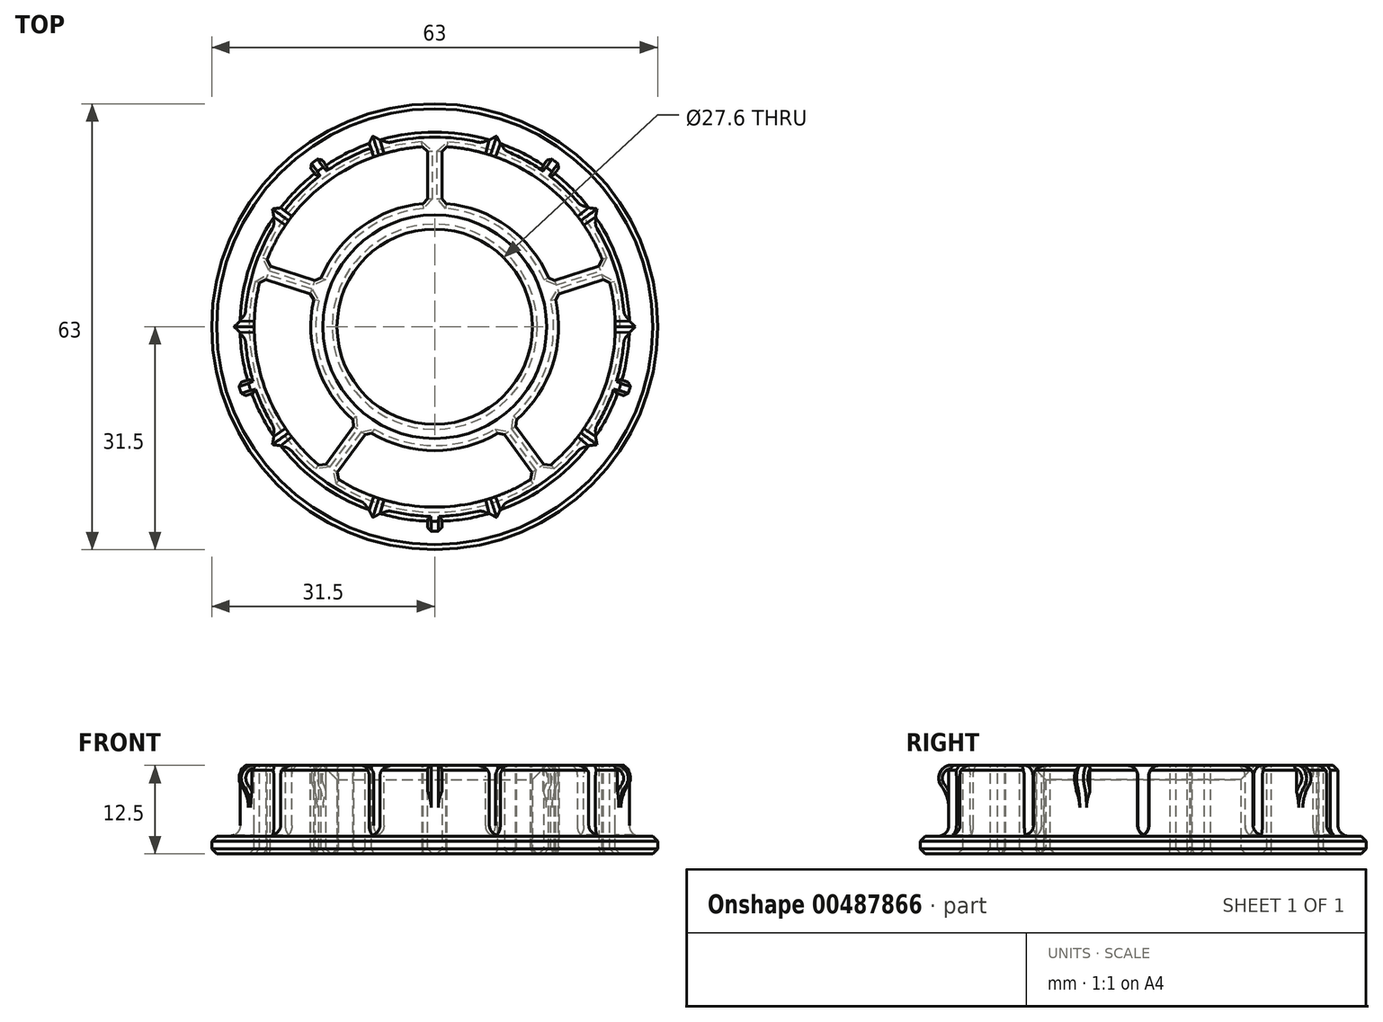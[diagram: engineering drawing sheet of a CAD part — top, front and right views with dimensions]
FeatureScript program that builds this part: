
annotation { "Feature Type Name" : "Feature", "Feature Type Description" : "" }
export const myFeature = defineFeature(function(context is Context, id is Id, definition is map)
    precondition{}
    {
        {
            var Q0;
            Q0=qCreatedBy(makeId("Front.planeOp"),FACE);
            var sketch = newSketch(context, id + "F0", { "sketchPlane" : qUnion([Q0])});
            skLineSegment(sketch, "E0", {"start": v(0, 0) * mm, "end": v(-63, 0) * mm, "construction": true});
            skLineSegment(sketch, "E1", {"start": v(-31.5, 0) * mm, "end": v(-31.5, 2.5) * mm});
            skLineSegment(sketch, "E2", {"start": v(-31.5, 2.5) * mm, "end": v(-27.5, 2.5) * mm});
            skLineSegment(sketch, "E3", {"start": v(-27.5, 2.5) * mm, "end": v(-27.5, 8.9) * mm});
            skLineSegment(sketch, "E4", {"start": v(-31.5, 0) * mm, "end": v(-13.8, 0) * mm});
            skLineSegment(sketch, "E5", {"start": v(-13.8, 0) * mm, "end": v(-13.8, 12.5) * mm});
            skLineSegment(sketch, "E6", {"start": v(-13.8, 12.5) * mm, "end": v(-27.5, 12.5) * mm});
            skLineSegment(sketch, "E7", {"start": v(0, 0) * mm, "end": v(0, 12.5) * mm, "construction": true});
            skLineSegment(sketch, "E8.0.MirrorCS", {"start": v(13.8, 0) * mm, "end": v(13.8, 12.5) * mm});
            skLineSegment(sketch, "E9.0.MirrorCS", {"start": v(13.8, 12.5) * mm, "end": v(27.5, 12.5) * mm});
            skLineSegment(sketch, "E10.0.MirrorCS", {"start": v(27.5, 2.5) * mm, "end": v(27.5, 12.5) * mm});
            skLineSegment(sketch, "E11.0.MirrorCS", {"start": v(31.5, 0) * mm, "end": v(31.5, 2.5) * mm});
            skLineSegment(sketch, "E12.0.MirrorCS", {"start": v(31.5, 0) * mm, "end": v(13.8, 0) * mm});
            skLineSegment(sketch, "E13.0.MirrorCS", {"start": v(31.5, 2.5) * mm, "end": v(27.5, 2.5) * mm});
            skArc(sketch, "E14", {"start": v(-27.5, 12.5) * mm, "mid": v(-28.9, 10.7) * mm, "end": v(-27.5, 8.9) * mm});
            skSolve(sketch);
        }
        {
            var Q0;
            Q0=makeQuery(id+"F0.imprint","IMPRINT",FACE,{"disambiguationData":[TD([[makeQuery(id+"F0.imprint","IMPRINT",EDGE,{"derivedFrom":sQuery(id+"F0.wireOp",EDGE,"E1")}),-1.0]])]});
            var Q1;
            Q1 = qSketchRegion(id + "F2", true);
            var Q2;
            Q2=sQuery(id+"F0.wireOp",EDGE,"E7");
            revolve(context, id + "F1", {"entities" : qUnion([Q0, Q1]), "axis" : qUnion([Q2]), "revolveType" : RevolveType.FULL});
        }
        {
            var Q0;
            Q0=makeQuery(id+"F1.opRevolve","SWEPT_FACE",FACE,{"disambiguationData":[OSD([sQuery(id+"F0.wireOp",EDGE,"E6")])]});
            var sketch = newSketch(context, id + "F2", { "sketchPlane" : qUnion([Q0])});
            skCircle(sketch, "E15.0", {"center": v(0, 0) * mm, "radius": 31.5 * mm});
            skCircle(sketch, "E15.1", {"center": v(0, 0) * mm, "radius": 13.8 * mm});
            skCircle(sketch, "E16.0", {"center": v(0, 0) * mm, "radius": 27.5 * mm});
            skCircle(sketch, "E17", {"center": v(0, 0) * mm, "radius": 17.5 * mm});
            skCircle(sketch, "E18", {"center": v(0, 0) * mm, "radius": 25.5 * mm});
            skLineSegment(sketch, "E19", {"start": v(0, 0) * mm, "end": v(0, 31.5) * mm, "construction": true});
            skLineSegment(sketch, "E20", {"start": v(-1, 17.47) * mm, "end": v(-1, 25.48) * mm});
            skLineSegment(sketch, "E21.0.MirrorCS", {"start": v(1, 17.47) * mm, "end": v(1, 25.48) * mm});
            skLineSegment(sketch, "E22.1.0", {"start": v(-16.93, 4.45) * mm, "end": v(-24.54, 6.92) * mm});
            skLineSegment(sketch, "E22.1.1", {"start": v(-16.3, 6.35) * mm, "end": v(-23.92, 8.82) * mm});
            skLineSegment(sketch, "E22.2.0", {"start": v(-9.46, -14.72) * mm, "end": v(-14.17, -21.2) * mm});
            skLineSegment(sketch, "E22.2.1", {"start": v(-11.08, -13.55) * mm, "end": v(-15.79, -20.03) * mm});
            skLineSegment(sketch, "E22.3.0", {"start": v(11.08, -13.55) * mm, "end": v(15.79, -20.03) * mm});
            skLineSegment(sketch, "E22.3.1", {"start": v(9.46, -14.72) * mm, "end": v(14.17, -21.2) * mm});
            skLineSegment(sketch, "E22.4.0", {"start": v(16.3, 6.35) * mm, "end": v(23.92, 8.82) * mm});
            skLineSegment(sketch, "E22.4.1", {"start": v(16.93, 4.45) * mm, "end": v(24.54, 6.92) * mm});
            skLineSegment(sketch, "E23", {"start": v(16.16, 22.25) * mm, "end": v(-16.16, -22.25) * mm, "construction": true});
            skLineSegment(sketch, "E24", {"start": v(15.34, 22.82) * mm, "end": v(17.7, 26.06) * mm});
            skLineSegment(sketch, "E25.0.MirrorCS", {"start": v(16.96, 21.65) * mm, "end": v(19.31, 24.88) * mm});
            skLineSegment(sketch, "E26.1.0", {"start": v(-16.96, 21.65) * mm, "end": v(-19.31, 24.88) * mm});
            skLineSegment(sketch, "E26.1.1", {"start": v(-15.34, 22.82) * mm, "end": v(-17.7, 26.06) * mm});
            skLineSegment(sketch, "E26.2.0", {"start": v(-25.83, -9.44) * mm, "end": v(-29.63, -10.68) * mm});
            skLineSegment(sketch, "E26.2.1", {"start": v(-26.45, -7.54) * mm, "end": v(-30.25, -8.78) * mm});
            skLineSegment(sketch, "E26.3.0", {"start": v(1, -27.48) * mm, "end": v(1, -31.48) * mm});
            skLineSegment(sketch, "E26.3.1", {"start": v(-1, -27.48) * mm, "end": v(-1, -31.48) * mm});
            skLineSegment(sketch, "E26.4.0", {"start": v(26.45, -7.54) * mm, "end": v(30.25, -8.78) * mm});
            skLineSegment(sketch, "E26.4.1", {"start": v(25.83, -9.44) * mm, "end": v(29.63, -10.68) * mm});
            skSolve(sketch);
        }
        {
            var Q0;
            {var subQ10=sQuery(id+"F2.wireOp",EDGE,"E16.0");var subQ16=makeQuery(id+"F2.imprint","INTERSECT",VERTEX,{"derivedFrom":[subQ10,sQuery(id+"F2.wireOp",EDGE,"E26.1.0")]});Q0=makeQuery(id+"F2.imprint","IMPRINT",FACE,{"disambiguationData":[TD([[makeQuery(id+"F2.imprint","IMPRINT",EDGE,{"disambiguationData":[TD([[subQ16,-1.0]])],"derivedFrom":subQ10}),-1.0]])]});}
            var sketch = newSketch(context, id + "F3", { "sketchPlane" : qUnion([Q0])});
            skLineSegment(sketch, "E27.0", {"start": v(0, 0) * mm, "end": v(0, 31.5) * mm, "construction": true});
            skLineSegment(sketch, "E27.1", {"start": v(16.16, 22.25) * mm, "end": v(-16.16, -22.25) * mm, "construction": true});
            skCircle(sketch, "E27.2", {"center": v(0, 0) * mm, "radius": 25.5 * mm});
            skCircle(sketch, "E27.3", {"center": v(0, 0) * mm, "radius": 27.5 * mm});
            skPoint(sketch, "E28", {"position": v(0, 27.5) * mm});
            skLineSegment(sketch, "E29", {"start": v(0, 27.5) * mm, "end": v(8.5, 26.15) * mm, "construction": true});
            skLineSegment(sketch, "E30", {"start": v(8.5, 26.15) * mm, "end": v(16.16, 22.25) * mm, "construction": true});
            skLineSegment(sketch, "E31", {"start": v(0, 0) * mm, "end": v(8.5, 26.15) * mm, "construction": true});
            skLineSegment(sketch, "E32", {"start": v(7.73, 26.4) * mm, "end": v(7.16, 24.47) * mm});
            skLineSegment(sketch, "E33.0.MirrorCS", {"start": v(9.26, 25.9) * mm, "end": v(8.59, 24) * mm});
            skLineSegment(sketch, "E34.1.0", {"start": v(-9.26, 25.9) * mm, "end": v(-8.59, 24) * mm});
            skLineSegment(sketch, "E34.1.1", {"start": v(-7.73, 26.4) * mm, "end": v(-7.16, 24.47) * mm});
            skLineSegment(sketch, "E34.2.0", {"start": v(-22.71, 15.5) * mm, "end": v(-21.06, 14.38) * mm});
            skLineSegment(sketch, "E34.2.1", {"start": v(-21.76, 16.81) * mm, "end": v(-20.18, 15.59) * mm});
            skLineSegment(sketch, "E34.3.0", {"start": v(-27.49, -0.8) * mm, "end": v(-25.49, -0.75) * mm});
            skLineSegment(sketch, "E34.3.1", {"start": v(-27.49, 0.8) * mm, "end": v(-25.49, 0.75) * mm});
            skLineSegment(sketch, "E34.4.0", {"start": v(-21.76, -16.81) * mm, "end": v(-20.18, -15.59) * mm});
            skLineSegment(sketch, "E34.4.1", {"start": v(-22.71, -15.5) * mm, "end": v(-21.06, -14.38) * mm});
            skLineSegment(sketch, "E34.5.0", {"start": v(-7.73, -26.4) * mm, "end": v(-7.16, -24.47) * mm});
            skLineSegment(sketch, "E34.5.1", {"start": v(-9.26, -25.9) * mm, "end": v(-8.59, -24) * mm});
            skLineSegment(sketch, "E34.6.0", {"start": v(9.26, -25.9) * mm, "end": v(8.59, -24) * mm});
            skLineSegment(sketch, "E34.6.1", {"start": v(7.73, -26.4) * mm, "end": v(7.16, -24.47) * mm});
            skLineSegment(sketch, "E34.7.0", {"start": v(22.71, -15.5) * mm, "end": v(21.06, -14.38) * mm});
            skLineSegment(sketch, "E34.7.1", {"start": v(21.76, -16.81) * mm, "end": v(20.18, -15.59) * mm});
            skLineSegment(sketch, "E34.8.0", {"start": v(27.49, 0.8) * mm, "end": v(25.49, 0.75) * mm});
            skLineSegment(sketch, "E34.8.1", {"start": v(27.49, -0.8) * mm, "end": v(25.49, -0.75) * mm});
            skLineSegment(sketch, "E34.9.0", {"start": v(21.76, 16.81) * mm, "end": v(20.18, 15.59) * mm});
            skLineSegment(sketch, "E34.9.1", {"start": v(22.71, 15.5) * mm, "end": v(21.06, 14.38) * mm});
            skSolve(sketch);
        }
        {
            var Q0;
            {var subQ2=sQuery(id+"F2.wireOp",EDGE,"E20");Q0=makeQuery(id+"F2.imprint","IMPRINT",FACE,{"disambiguationData":[TD([[makeQuery(id+"F2.imprint","IMPRINT",EDGE,{"derivedFrom":subQ2}),1.0]])]});}
            var Q1;
            {var subQ1=sQuery(id+"F2.wireOp",EDGE,"E21.0.MirrorCS");Q1=makeQuery(id+"F2.imprint","IMPRINT",FACE,{"disambiguationData":[TD([[makeQuery(id+"F2.imprint","IMPRINT",EDGE,{"derivedFrom":subQ1}),-1.0]])]});}
            var Q2;
            {var subQ1=sQuery(id+"F2.wireOp",EDGE,"E22.3.0");Q2=makeQuery(id+"F2.imprint","IMPRINT",FACE,{"disambiguationData":[TD([[makeQuery(id+"F2.imprint","IMPRINT",EDGE,{"derivedFrom":subQ1}),1.0]])]});}
            var Q3;
            {var subQ2=sQuery(id+"F2.wireOp",EDGE,"E22.2.0");Q3=makeQuery(id+"F2.imprint","IMPRINT",FACE,{"disambiguationData":[TD([[makeQuery(id+"F2.imprint","IMPRINT",EDGE,{"derivedFrom":subQ2}),1.0]])]});}
            var Q4;
            {var subQ1=sQuery(id+"F2.wireOp",EDGE,"E22.1.0");Q4=makeQuery(id+"F2.imprint","IMPRINT",FACE,{"disambiguationData":[TD([[makeQuery(id+"F2.imprint","IMPRINT",EDGE,{"derivedFrom":subQ1}),1.0]])]});}
            var Q5;
            Q5=makeQuery(id+"F1.opRevolve","SWEPT_FACE",FACE,{"disambiguationData":[OSD([sQuery(id+"F0.wireOp",EDGE,"E4")])]});
            extrude(context, id + "F4", {"entities" : qUnion([Q0, Q1, Q2, Q3, Q4]), "operationType" : NewBodyOperationType.REMOVE, "endBound" : BoundingType.UP_TO_SURFACE, "oppositeDirection" : true, "endBoundEntityFace" : qUnion([Q5]), "depth" : 25 * mm});
        }
        {
            var Q0;
            {var subQ0=sQuery(id+"F2.wireOp",EDGE,"E24");Q0=makeQuery(id+"F2.imprint","IMPRINT",FACE,{"disambiguationData":[TD([[makeQuery(id+"F2.imprint","IMPRINT",EDGE,{"derivedFrom":subQ0}),1.0]])]});}
            var Q1;
            {var subQ1=sQuery(id+"F2.wireOp",EDGE,"E25.0.MirrorCS");Q1=makeQuery(id+"F2.imprint","IMPRINT",FACE,{"disambiguationData":[TD([[makeQuery(id+"F2.imprint","IMPRINT",EDGE,{"derivedFrom":subQ1}),-1.0]])]});}
            var Q2;
            {var subQ1=sQuery(id+"F2.wireOp",EDGE,"E26.3.0");Q2=makeQuery(id+"F2.imprint","IMPRINT",FACE,{"disambiguationData":[TD([[makeQuery(id+"F2.imprint","IMPRINT",EDGE,{"derivedFrom":subQ1}),1.0]])]});}
            var Q3;
            {var subQ1=sQuery(id+"F2.wireOp",EDGE,"E26.2.0");Q3=makeQuery(id+"F2.imprint","IMPRINT",FACE,{"disambiguationData":[TD([[makeQuery(id+"F2.imprint","IMPRINT",EDGE,{"derivedFrom":subQ1}),1.0]])]});}
            var Q4;
            {var subQ1=sQuery(id+"F2.wireOp",EDGE,"E26.1.0");Q4=makeQuery(id+"F2.imprint","IMPRINT",FACE,{"disambiguationData":[TD([[makeQuery(id+"F2.imprint","IMPRINT",EDGE,{"derivedFrom":subQ1}),1.0]])]});}
            extrude(context, id + "F5", {"entities" : qUnion([Q0, Q1, Q2, Q3, Q4]), "operationType" : NewBodyOperationType.REMOVE, "endBound" : BoundingType.UP_TO_NEXT, "oppositeDirection" : true, "depth" : 25 * mm});
        }
        {
            var Q0;
            {var subQ1=sQuery(id+"F3.wireOp",EDGE,"E34.1.0");Q0=makeQuery(id+"F3.imprint","IMPRINT",FACE,{"disambiguationData":[TD([[makeQuery(id+"F3.imprint","IMPRINT",EDGE,{"derivedFrom":subQ1}),1.0]])]});}
            var Q1;
            {var subQ1=sQuery(id+"F3.wireOp",EDGE,"E34.2.0");Q1=makeQuery(id+"F3.imprint","IMPRINT",FACE,{"disambiguationData":[TD([[makeQuery(id+"F3.imprint","IMPRINT",EDGE,{"derivedFrom":subQ1}),1.0]])]});}
            var Q2;
            {var subQ1=sQuery(id+"F3.wireOp",EDGE,"E34.3.0");Q2=makeQuery(id+"F3.imprint","IMPRINT",FACE,{"disambiguationData":[TD([[makeQuery(id+"F3.imprint","IMPRINT",EDGE,{"derivedFrom":subQ1}),1.0]])]});}
            var Q3;
            {var subQ1=sQuery(id+"F3.wireOp",EDGE,"E34.4.0");Q3=makeQuery(id+"F3.imprint","IMPRINT",FACE,{"disambiguationData":[TD([[makeQuery(id+"F3.imprint","IMPRINT",EDGE,{"derivedFrom":subQ1}),1.0]])]});}
            var Q4;
            {var subQ1=sQuery(id+"F3.wireOp",EDGE,"E34.5.0");Q4=makeQuery(id+"F3.imprint","IMPRINT",FACE,{"disambiguationData":[TD([[makeQuery(id+"F3.imprint","IMPRINT",EDGE,{"derivedFrom":subQ1}),1.0]])]});}
            var Q5;
            {var subQ1=sQuery(id+"F3.wireOp",EDGE,"E34.6.0");Q5=makeQuery(id+"F3.imprint","IMPRINT",FACE,{"disambiguationData":[TD([[makeQuery(id+"F3.imprint","IMPRINT",EDGE,{"derivedFrom":subQ1}),1.0]])]});}
            var Q6;
            {var subQ1=sQuery(id+"F3.wireOp",EDGE,"E34.7.0");Q6=makeQuery(id+"F3.imprint","IMPRINT",FACE,{"disambiguationData":[TD([[makeQuery(id+"F3.imprint","IMPRINT",EDGE,{"derivedFrom":subQ1}),1.0]])]});}
            var Q7;
            {var subQ1=sQuery(id+"F3.wireOp",EDGE,"E34.8.0");Q7=makeQuery(id+"F3.imprint","IMPRINT",FACE,{"disambiguationData":[TD([[makeQuery(id+"F3.imprint","IMPRINT",EDGE,{"derivedFrom":subQ1}),1.0]])]});}
            var Q8;
            {var subQ1=sQuery(id+"F3.wireOp",EDGE,"E34.9.0");Q8=makeQuery(id+"F3.imprint","IMPRINT",FACE,{"disambiguationData":[TD([[makeQuery(id+"F3.imprint","IMPRINT",EDGE,{"derivedFrom":subQ1}),1.0]])]});}
            var Q9;
            {var subQ1=sQuery(id+"F3.wireOp",EDGE,"E32");Q9=makeQuery(id+"F3.imprint","IMPRINT",FACE,{"disambiguationData":[TD([[makeQuery(id+"F3.imprint","IMPRINT",EDGE,{"derivedFrom":subQ1}),1.0]])]});}
            var Q10;
            Q10=makeQuery(id+"F1.opRevolve","SWEPT_FACE",FACE,{"disambiguationData":[OSD([sQuery(id+"F0.wireOp",EDGE,"E2")])]});
            extrude(context, id + "F6", {"entities" : qUnion([Q0, Q1, Q2, Q3, Q4, Q5, Q6, Q7, Q8, Q9]), "operationType" : NewBodyOperationType.REMOVE, "endBound" : BoundingType.UP_TO_SURFACE, "oppositeDirection" : true, "endBoundEntityFace" : qUnion([Q10]), "depth" : 10 * mm});
        }
        {
            var Q0;
            {var subQ0=sQuery(id+"F0.wireOp",EDGE,"E6");var subQ1=sQuery(id+"F0.wireOp",EDGE,"E14");var subQ2=makeQuery(id+"F1.opRevolve","SWEPT_EDGE",EDGE,{"disambiguationData":[OSD([subQ0,subQ1])]});var subQ3=sQuery(id+"F2.wireOp",EDGE,"E16.0");Q0=makeQuery(id+"F5.boolean.opBoolean","MERGE",EDGE,{"derivedFrom":[subQ2,makeQuery(id+"F5.opExtrude","CAP_EDGE",EDGE,{"disambiguationData":[OSD([subQ0,subQ1,subQ3]),TDD([subQ2,makeQuery(id+"F2.imprint","IMPRINT",EDGE,{"disambiguationData":[TD([[makeQuery(id+"F2.imprint","INTERSECT",VERTEX,{"derivedFrom":[subQ3,sQuery(id+"F2.wireOp",EDGE,"E26.1.0")]}),1.0]])],"derivedFrom":subQ3})])],"isStart":true})]});}
            var Q1;
            {var subQ0=sQuery(id+"F0.wireOp",EDGE,"E6");var subQ1=sQuery(id+"F0.wireOp",EDGE,"E14");var subQ2=makeQuery(id+"F1.opRevolve","SWEPT_EDGE",EDGE,{"disambiguationData":[OSD([subQ0,subQ1])]});var subQ3=sQuery(id+"F2.wireOp",EDGE,"E16.0");Q1=makeQuery(id+"F5.boolean.opBoolean","MERGE",EDGE,{"derivedFrom":[subQ2,makeQuery(id+"F5.opExtrude","CAP_EDGE",EDGE,{"disambiguationData":[OSD([subQ0,subQ1,subQ3]),TDD([subQ2,makeQuery(id+"F2.imprint","IMPRINT",EDGE,{"disambiguationData":[TD([[makeQuery(id+"F2.imprint","INTERSECT",VERTEX,{"derivedFrom":[subQ3,sQuery(id+"F2.wireOp",EDGE,"E26.2.0")]}),1.0]])],"derivedFrom":subQ3})])],"isStart":true})]});}
            var Q2;
            {var subQ0=sQuery(id+"F0.wireOp",EDGE,"E6");var subQ1=sQuery(id+"F0.wireOp",EDGE,"E14");var subQ2=makeQuery(id+"F1.opRevolve","SWEPT_EDGE",EDGE,{"disambiguationData":[OSD([subQ0,subQ1])]});var subQ3=sQuery(id+"F2.wireOp",EDGE,"E16.0");Q2=makeQuery(id+"F5.boolean.opBoolean","MERGE",EDGE,{"derivedFrom":[subQ2,makeQuery(id+"F5.opExtrude","CAP_EDGE",EDGE,{"disambiguationData":[OSD([subQ0,subQ1,subQ3]),TDD([subQ2,makeQuery(id+"F2.imprint","IMPRINT",EDGE,{"disambiguationData":[TD([[makeQuery(id+"F2.imprint","INTERSECT",VERTEX,{"derivedFrom":[subQ3,sQuery(id+"F2.wireOp",EDGE,"E26.3.0")]}),1.0]])],"derivedFrom":subQ3})])],"isStart":true})]});}
            var Q3;
            {var subQ0=sQuery(id+"F0.wireOp",EDGE,"E6");var subQ1=sQuery(id+"F0.wireOp",EDGE,"E14");var subQ2=makeQuery(id+"F1.opRevolve","SWEPT_EDGE",EDGE,{"disambiguationData":[OSD([subQ0,subQ1])]});var subQ3=sQuery(id+"F2.wireOp",EDGE,"E16.0");Q3=makeQuery(id+"F5.boolean.opBoolean","MERGE",EDGE,{"derivedFrom":[subQ2,makeQuery(id+"F5.opExtrude","CAP_EDGE",EDGE,{"disambiguationData":[OSD([subQ0,subQ1,subQ3]),TDD([subQ2,makeQuery(id+"F2.imprint","IMPRINT",EDGE,{"disambiguationData":[TD([[makeQuery(id+"F2.imprint","INTERSECT",VERTEX,{"derivedFrom":[subQ3,sQuery(id+"F2.wireOp",EDGE,"E25.0.MirrorCS")]}),-1.0]])],"derivedFrom":subQ3})])],"isStart":true})]});}
            var Q4;
            {var subQ0=sQuery(id+"F0.wireOp",EDGE,"E6");var subQ1=sQuery(id+"F0.wireOp",EDGE,"E14");var subQ2=makeQuery(id+"F1.opRevolve","SWEPT_EDGE",EDGE,{"disambiguationData":[OSD([subQ0,subQ1])]});var subQ3=sQuery(id+"F2.wireOp",EDGE,"E16.0");Q4=makeQuery(id+"F5.boolean.opBoolean","MERGE",EDGE,{"derivedFrom":[subQ2,makeQuery(id+"F5.opExtrude","CAP_EDGE",EDGE,{"disambiguationData":[OSD([subQ0,subQ1,subQ3]),TDD([subQ2,makeQuery(id+"F2.imprint","IMPRINT",EDGE,{"disambiguationData":[TD([[makeQuery(id+"F2.imprint","INTERSECT",VERTEX,{"derivedFrom":[subQ3,sQuery(id+"F2.wireOp",EDGE,"E24")]}),1.0]])],"derivedFrom":subQ3})])],"isStart":true})]});}
            var Q5;
            {var subQ0=sQuery(id+"F2.wireOp",EDGE,"E18");Q5=makeQuery(id+"F4.boolean.opBoolean","COPY",EDGE,{"derivedFrom":makeQuery(id+"F4.opExtrude","CAP_EDGE",EDGE,{"disambiguationData":[OSD([subQ0]),TDD([makeQuery(id+"F2.imprint","IMPRINT",EDGE,{"disambiguationData":[TD([[makeQuery(id+"F2.imprint","INTERSECT",VERTEX,{"derivedFrom":[subQ0,sQuery(id+"F2.wireOp",EDGE,"E20")]}),-1.0]])],"derivedFrom":subQ0})])],"isStart":true})});}
            var Q6;
            Q6=makeQuery(id+"F4.boolean.opBoolean","COPY",EDGE,{"derivedFrom":makeQuery(id+"F4.opExtrude","CAP_EDGE",EDGE,{"disambiguationData":[OSD([sQuery(id+"F2.wireOp",EDGE,"E22.1.1")])],"isStart":true})});
            var Q7;
            {var subQ0=sQuery(id+"F2.wireOp",EDGE,"E17");Q7=makeQuery(id+"F4.boolean.opBoolean","COPY",EDGE,{"derivedFrom":makeQuery(id+"F4.opExtrude","CAP_EDGE",EDGE,{"disambiguationData":[OSD([subQ0]),TDD([makeQuery(id+"F2.imprint","IMPRINT",EDGE,{"disambiguationData":[TD([[makeQuery(id+"F2.imprint","INTERSECT",VERTEX,{"derivedFrom":[subQ0,sQuery(id+"F2.wireOp",EDGE,"E20")]}),-1.0]])],"derivedFrom":subQ0})])],"isStart":true})});}
            var Q8;
            Q8=makeQuery(id+"F4.boolean.opBoolean","COPY",EDGE,{"derivedFrom":makeQuery(id+"F4.opExtrude","CAP_EDGE",EDGE,{"disambiguationData":[OSD([sQuery(id+"F2.wireOp",EDGE,"E20")])],"isStart":true})});
            var Q9;
            Q9=makeQuery(id+"F4.boolean.opBoolean","COPY",EDGE,{"derivedFrom":makeQuery(id+"F4.opExtrude","CAP_EDGE",EDGE,{"disambiguationData":[OSD([sQuery(id+"F2.wireOp",EDGE,"E22.1.0")])],"isStart":true})});
            var Q10;
            {var subQ0=sQuery(id+"F2.wireOp",EDGE,"E18");Q10=makeQuery(id+"F4.boolean.opBoolean","COPY",EDGE,{"derivedFrom":makeQuery(id+"F4.opExtrude","CAP_EDGE",EDGE,{"disambiguationData":[OSD([subQ0]),TDD([makeQuery(id+"F2.imprint","IMPRINT",EDGE,{"disambiguationData":[TD([[makeQuery(id+"F2.imprint","INTERSECT",VERTEX,{"derivedFrom":[subQ0,sQuery(id+"F2.wireOp",EDGE,"E22.1.0")]}),-1.0]])],"derivedFrom":subQ0})])],"isStart":true})});}
            var Q11;
            Q11=makeQuery(id+"F4.boolean.opBoolean","COPY",EDGE,{"derivedFrom":makeQuery(id+"F4.opExtrude","CAP_EDGE",EDGE,{"disambiguationData":[OSD([sQuery(id+"F2.wireOp",EDGE,"E22.2.1")])],"isStart":true})});
            var Q12;
            {var subQ0=sQuery(id+"F2.wireOp",EDGE,"E17");Q12=makeQuery(id+"F4.boolean.opBoolean","COPY",EDGE,{"derivedFrom":makeQuery(id+"F4.opExtrude","CAP_EDGE",EDGE,{"disambiguationData":[OSD([subQ0]),TDD([makeQuery(id+"F2.imprint","IMPRINT",EDGE,{"disambiguationData":[TD([[makeQuery(id+"F2.imprint","INTERSECT",VERTEX,{"derivedFrom":[subQ0,sQuery(id+"F2.wireOp",EDGE,"E22.1.0")]}),-1.0]])],"derivedFrom":subQ0})])],"isStart":true})});}
            var Q13;
            Q13=makeQuery(id+"F4.boolean.opBoolean","COPY",EDGE,{"derivedFrom":makeQuery(id+"F4.opExtrude","CAP_EDGE",EDGE,{"disambiguationData":[OSD([sQuery(id+"F2.wireOp",EDGE,"E22.2.0")])],"isStart":true})});
            var Q14;
            {var subQ0=sQuery(id+"F2.wireOp",EDGE,"E18");Q14=makeQuery(id+"F4.boolean.opBoolean","COPY",EDGE,{"derivedFrom":makeQuery(id+"F4.opExtrude","CAP_EDGE",EDGE,{"disambiguationData":[OSD([subQ0]),TDD([makeQuery(id+"F2.imprint","IMPRINT",EDGE,{"disambiguationData":[TD([[makeQuery(id+"F2.imprint","INTERSECT",VERTEX,{"derivedFrom":[subQ0,sQuery(id+"F2.wireOp",EDGE,"E22.2.0")]}),-1.0]])],"derivedFrom":subQ0})])],"isStart":true})});}
            var Q15;
            {var subQ0=sQuery(id+"F2.wireOp",EDGE,"E17");Q15=makeQuery(id+"F4.boolean.opBoolean","COPY",EDGE,{"derivedFrom":makeQuery(id+"F4.opExtrude","CAP_EDGE",EDGE,{"disambiguationData":[OSD([subQ0]),TDD([makeQuery(id+"F2.imprint","IMPRINT",EDGE,{"disambiguationData":[TD([[makeQuery(id+"F2.imprint","INTERSECT",VERTEX,{"derivedFrom":[subQ0,sQuery(id+"F2.wireOp",EDGE,"E22.2.0")]}),-1.0]])],"derivedFrom":subQ0})])],"isStart":true})});}
            var Q16;
            Q16=makeQuery(id+"F4.boolean.opBoolean","COPY",EDGE,{"derivedFrom":makeQuery(id+"F4.opExtrude","CAP_EDGE",EDGE,{"disambiguationData":[OSD([sQuery(id+"F2.wireOp",EDGE,"E22.3.1")])],"isStart":true})});
            var Q17;
            Q17=makeQuery(id+"F4.boolean.opBoolean","COPY",EDGE,{"derivedFrom":makeQuery(id+"F4.opExtrude","CAP_EDGE",EDGE,{"disambiguationData":[OSD([sQuery(id+"F2.wireOp",EDGE,"E22.3.0")])],"isStart":true})});
            var Q18;
            {var subQ0=sQuery(id+"F2.wireOp",EDGE,"E17");Q18=makeQuery(id+"F4.boolean.opBoolean","COPY",EDGE,{"derivedFrom":makeQuery(id+"F4.opExtrude","CAP_EDGE",EDGE,{"disambiguationData":[OSD([subQ0]),TDD([makeQuery(id+"F2.imprint","IMPRINT",EDGE,{"disambiguationData":[TD([[makeQuery(id+"F2.imprint","INTERSECT",VERTEX,{"derivedFrom":[subQ0,sQuery(id+"F2.wireOp",EDGE,"E22.3.0")]}),-1.0]])],"derivedFrom":subQ0})])],"isStart":true})});}
            var Q19;
            {var subQ0=sQuery(id+"F2.wireOp",EDGE,"E18");Q19=makeQuery(id+"F4.boolean.opBoolean","COPY",EDGE,{"derivedFrom":makeQuery(id+"F4.opExtrude","CAP_EDGE",EDGE,{"disambiguationData":[OSD([subQ0]),TDD([makeQuery(id+"F2.imprint","IMPRINT",EDGE,{"disambiguationData":[TD([[makeQuery(id+"F2.imprint","INTERSECT",VERTEX,{"derivedFrom":[subQ0,sQuery(id+"F2.wireOp",EDGE,"E22.3.0")]}),-1.0]])],"derivedFrom":subQ0})])],"isStart":true})});}
            var Q20;
            Q20=makeQuery(id+"F4.boolean.opBoolean","COPY",EDGE,{"derivedFrom":makeQuery(id+"F4.opExtrude","CAP_EDGE",EDGE,{"disambiguationData":[OSD([sQuery(id+"F2.wireOp",EDGE,"E22.4.1")])],"isStart":true})});
            var Q21;
            Q21=makeQuery(id+"F4.boolean.opBoolean","COPY",EDGE,{"derivedFrom":makeQuery(id+"F4.opExtrude","CAP_EDGE",EDGE,{"disambiguationData":[OSD([sQuery(id+"F2.wireOp",EDGE,"E22.4.0")])],"isStart":true})});
            var Q22;
            {var subQ0=sQuery(id+"F2.wireOp",EDGE,"E17");Q22=makeQuery(id+"F4.boolean.opBoolean","COPY",EDGE,{"derivedFrom":makeQuery(id+"F4.opExtrude","CAP_EDGE",EDGE,{"disambiguationData":[OSD([subQ0]),TDD([makeQuery(id+"F2.imprint","IMPRINT",EDGE,{"disambiguationData":[TD([[makeQuery(id+"F2.imprint","INTERSECT",VERTEX,{"derivedFrom":[subQ0,sQuery(id+"F2.wireOp",EDGE,"E21.0.MirrorCS")]}),1.0]])],"derivedFrom":subQ0})])],"isStart":true})});}
            var Q23;
            {var subQ0=sQuery(id+"F2.wireOp",EDGE,"E18");Q23=makeQuery(id+"F4.boolean.opBoolean","COPY",EDGE,{"derivedFrom":makeQuery(id+"F4.opExtrude","CAP_EDGE",EDGE,{"disambiguationData":[OSD([subQ0]),TDD([makeQuery(id+"F2.imprint","IMPRINT",EDGE,{"disambiguationData":[TD([[makeQuery(id+"F2.imprint","INTERSECT",VERTEX,{"derivedFrom":[subQ0,sQuery(id+"F2.wireOp",EDGE,"E21.0.MirrorCS")]}),1.0]])],"derivedFrom":subQ0})])],"isStart":true})});}
            var Q24;
            Q24=makeQuery(id+"F4.boolean.opBoolean","COPY",EDGE,{"derivedFrom":makeQuery(id+"F4.opExtrude","CAP_EDGE",EDGE,{"disambiguationData":[OSD([sQuery(id+"F2.wireOp",EDGE,"E21.0.MirrorCS")])],"isStart":true})});
            var Q25;
            Q25=makeQuery(id+"F1.opRevolve","SWEPT_EDGE",EDGE,{"disambiguationData":[OSD([sQuery(id+"F0.wireOp",EDGE,"E1"),sQuery(id+"F0.wireOp",EDGE,"E2")])]});
            var Q26;
            Q26=makeQuery(id+"F1.opRevolve","SWEPT_EDGE",EDGE,{"disambiguationData":[OSD([sQuery(id+"F0.wireOp",EDGE,"E1"),sQuery(id+"F0.wireOp",EDGE,"E4")])]});
            var Q27;
            Q27=makeQuery(id+"F4.boolean.opBoolean","COPY",EDGE,{"derivedFrom":makeQuery(id+"F4.opExtrude","SWEPT_EDGE",EDGE,{"disambiguationData":[OSD([sQuery(id+"F2.wireOp",EDGE,"E18"),sQuery(id+"F2.wireOp",EDGE,"E22.4.0")])]})});
            var Q28;
            Q28=makeQuery(id+"F4.boolean.opBoolean","COPY",EDGE,{"derivedFrom":makeQuery(id+"F4.opExtrude","SWEPT_EDGE",EDGE,{"disambiguationData":[OSD([sQuery(id+"F2.wireOp",EDGE,"E18"),sQuery(id+"F2.wireOp",EDGE,"E22.4.1")])]})});
            var Q29;
            Q29=makeQuery(id+"F4.boolean.opBoolean","COPY",EDGE,{"derivedFrom":makeQuery(id+"F4.opExtrude","SWEPT_EDGE",EDGE,{"disambiguationData":[OSD([sQuery(id+"F2.wireOp",EDGE,"E18"),sQuery(id+"F2.wireOp",EDGE,"E22.3.0")])]})});
            var Q30;
            Q30=makeQuery(id+"F4.boolean.opBoolean","COPY",EDGE,{"derivedFrom":makeQuery(id+"F4.opExtrude","SWEPT_EDGE",EDGE,{"disambiguationData":[OSD([sQuery(id+"F2.wireOp",EDGE,"E18"),sQuery(id+"F2.wireOp",EDGE,"E22.3.1")])]})});
            var Q31;
            Q31=makeQuery(id+"F4.boolean.opBoolean","COPY",EDGE,{"derivedFrom":makeQuery(id+"F4.opExtrude","SWEPT_EDGE",EDGE,{"disambiguationData":[OSD([sQuery(id+"F2.wireOp",EDGE,"E18"),sQuery(id+"F2.wireOp",EDGE,"E22.2.0")])]})});
            var Q32;
            Q32=makeQuery(id+"F4.boolean.opBoolean","COPY",EDGE,{"derivedFrom":makeQuery(id+"F4.opExtrude","SWEPT_EDGE",EDGE,{"disambiguationData":[OSD([sQuery(id+"F2.wireOp",EDGE,"E18"),sQuery(id+"F2.wireOp",EDGE,"E22.2.1")])]})});
            var Q33;
            Q33=makeQuery(id+"F4.boolean.opBoolean","COPY",EDGE,{"derivedFrom":makeQuery(id+"F4.opExtrude","SWEPT_EDGE",EDGE,{"disambiguationData":[OSD([sQuery(id+"F2.wireOp",EDGE,"E17"),sQuery(id+"F2.wireOp",EDGE,"E22.1.0")])]})});
            var Q34;
            Q34=makeQuery(id+"F4.boolean.opBoolean","COPY",EDGE,{"derivedFrom":makeQuery(id+"F4.opExtrude","SWEPT_EDGE",EDGE,{"disambiguationData":[OSD([sQuery(id+"F2.wireOp",EDGE,"E17"),sQuery(id+"F2.wireOp",EDGE,"E22.1.1")])]})});
            var Q35;
            Q35=makeQuery(id+"F4.boolean.opBoolean","COPY",EDGE,{"derivedFrom":makeQuery(id+"F4.opExtrude","SWEPT_EDGE",EDGE,{"disambiguationData":[OSD([sQuery(id+"F2.wireOp",EDGE,"E17"),sQuery(id+"F2.wireOp",EDGE,"E20")])]})});
            var Q36;
            Q36=makeQuery(id+"F4.boolean.opBoolean","COPY",EDGE,{"derivedFrom":makeQuery(id+"F4.opExtrude","SWEPT_EDGE",EDGE,{"disambiguationData":[OSD([sQuery(id+"F2.wireOp",EDGE,"E17"),sQuery(id+"F2.wireOp",EDGE,"E21.0.MirrorCS")])]})});
            var Q37;
            Q37=makeQuery(id+"F4.boolean.opBoolean","COPY",EDGE,{"derivedFrom":makeQuery(id+"F4.opExtrude","SWEPT_EDGE",EDGE,{"disambiguationData":[OSD([sQuery(id+"F2.wireOp",EDGE,"E17"),sQuery(id+"F2.wireOp",EDGE,"E22.4.0")])]})});
            var Q38;
            Q38=makeQuery(id+"F4.boolean.opBoolean","COPY",EDGE,{"derivedFrom":makeQuery(id+"F4.opExtrude","SWEPT_EDGE",EDGE,{"disambiguationData":[OSD([sQuery(id+"F2.wireOp",EDGE,"E17"),sQuery(id+"F2.wireOp",EDGE,"E22.4.1")])]})});
            var Q39;
            Q39=makeQuery(id+"F4.boolean.opBoolean","COPY",EDGE,{"derivedFrom":makeQuery(id+"F4.opExtrude","SWEPT_EDGE",EDGE,{"disambiguationData":[OSD([sQuery(id+"F2.wireOp",EDGE,"E18"),sQuery(id+"F2.wireOp",EDGE,"E21.0.MirrorCS")])]})});
            var Q40;
            Q40=makeQuery(id+"F4.boolean.opBoolean","COPY",EDGE,{"derivedFrom":makeQuery(id+"F4.opExtrude","SWEPT_EDGE",EDGE,{"disambiguationData":[OSD([sQuery(id+"F2.wireOp",EDGE,"E18"),sQuery(id+"F2.wireOp",EDGE,"E20")])]})});
            var Q41;
            Q41=makeQuery(id+"F4.boolean.opBoolean","COPY",EDGE,{"derivedFrom":makeQuery(id+"F4.opExtrude","SWEPT_EDGE",EDGE,{"disambiguationData":[OSD([sQuery(id+"F2.wireOp",EDGE,"E18"),sQuery(id+"F2.wireOp",EDGE,"E22.1.0")])]})});
            var Q42;
            Q42=makeQuery(id+"F4.boolean.opBoolean","COPY",EDGE,{"derivedFrom":makeQuery(id+"F4.opExtrude","SWEPT_EDGE",EDGE,{"disambiguationData":[OSD([sQuery(id+"F2.wireOp",EDGE,"E18"),sQuery(id+"F2.wireOp",EDGE,"E22.1.1")])]})});
            var Q43;
            Q43=makeQuery(id+"F4.boolean.opBoolean","COPY",EDGE,{"derivedFrom":makeQuery(id+"F4.opExtrude","SWEPT_EDGE",EDGE,{"disambiguationData":[OSD([sQuery(id+"F2.wireOp",EDGE,"E17"),sQuery(id+"F2.wireOp",EDGE,"E22.3.1")])]})});
            var Q44;
            Q44=makeQuery(id+"F4.boolean.opBoolean","COPY",EDGE,{"derivedFrom":makeQuery(id+"F4.opExtrude","SWEPT_EDGE",EDGE,{"disambiguationData":[OSD([sQuery(id+"F2.wireOp",EDGE,"E17"),sQuery(id+"F2.wireOp",EDGE,"E22.2.0")])]})});
            var Q45;
            Q45=makeQuery(id+"F4.boolean.opBoolean","COPY",EDGE,{"derivedFrom":makeQuery(id+"F4.opExtrude","SWEPT_EDGE",EDGE,{"disambiguationData":[OSD([sQuery(id+"F2.wireOp",EDGE,"E17"),sQuery(id+"F2.wireOp",EDGE,"E22.2.1")])]})});
            var Q46;
            Q46=makeQuery(id+"F4.boolean.opBoolean","COPY",EDGE,{"derivedFrom":makeQuery(id+"F4.opExtrude","SWEPT_EDGE",EDGE,{"disambiguationData":[OSD([sQuery(id+"F2.wireOp",EDGE,"E17"),sQuery(id+"F2.wireOp",EDGE,"E22.3.0")])]})});
            var Q47;
            Q47=makeQuery(id+"F1.opRevolve","SWEPT_FACE",FACE,{"disambiguationData":[OSD([sQuery(id+"F0.wireOp",EDGE,"E4")])]});
            chamfer(context, id + "F7", {"entities" : qUnion([Q0, Q1, Q2, Q3, Q4, Q5, Q6, Q7, Q8, Q9, Q10, Q11, Q12, Q13, Q14, Q15, Q16, Q17, Q18, Q19, Q20, Q21, Q22, Q23, Q24, Q25, Q26, Q27, Q28, Q29, Q30, Q31, Q32, Q33, Q34, Q35, Q36, Q37, Q38, Q39, Q40, Q41, Q42, Q43, Q44, Q45, Q46, Q47]), "width" : 0.7 * mm, "tangentPropagation" : true});
        }
        {
            var Q0;
            Q0=makeQuery(id+"F1.opRevolve","SWEPT_EDGE",EDGE,{"disambiguationData":[OSD([sQuery(id+"F0.wireOp",EDGE,"E5"),sQuery(id+"F0.wireOp",EDGE,"E6")])]});
            chamfer(context, id + "F8", {"entities" : qUnion([Q0]), "width" : 2 * mm, "tangentPropagation" : true});
        }
        {
            var Q0;
            {var subQ0=sQuery(id+"F0.wireOp",EDGE,"E3");var subQ1=sQuery(id+"F0.wireOp",EDGE,"E14");var subQ3=sQuery(id+"F2.wireOp",EDGE,"E26.4.0");Q0=makeQuery(id+"F5.boolean.opBoolean","SPLIT",EDGE,{"disambiguationData":[TD([makeQuery(id+"F5.opExtrude","SWEPT_FACE",FACE,{"disambiguationData":[OSD([subQ3])]})])],"derivedFrom":makeQuery(id+"F1.opRevolve","SWEPT_EDGE",EDGE,{"disambiguationData":[OSD([subQ0,subQ1])]})});}
            var Q1;
            {var subQ0=sQuery(id+"F0.wireOp",EDGE,"E3");var subQ1=sQuery(id+"F0.wireOp",EDGE,"E14");var subQ3=sQuery(id+"F2.wireOp",EDGE,"E24");Q1=makeQuery(id+"F5.boolean.opBoolean","SPLIT",EDGE,{"disambiguationData":[TD([makeQuery(id+"F5.opExtrude","SWEPT_FACE",FACE,{"disambiguationData":[OSD([subQ3])]})])],"derivedFrom":makeQuery(id+"F1.opRevolve","SWEPT_EDGE",EDGE,{"disambiguationData":[OSD([subQ0,subQ1])]})});}
            var Q2;
            {var subQ0=sQuery(id+"F0.wireOp",EDGE,"E3");var subQ1=sQuery(id+"F0.wireOp",EDGE,"E14");var subQ2=sQuery(id+"F2.wireOp",EDGE,"E26.1.0");Q2=makeQuery(id+"F5.boolean.opBoolean","SPLIT",EDGE,{"disambiguationData":[TD([makeQuery(id+"F5.opExtrude","SWEPT_FACE",FACE,{"disambiguationData":[OSD([subQ2])]})])],"derivedFrom":makeQuery(id+"F1.opRevolve","SWEPT_EDGE",EDGE,{"disambiguationData":[OSD([subQ0,subQ1])]})});}
            var Q3;
            {var subQ0=sQuery(id+"F0.wireOp",EDGE,"E3");var subQ1=sQuery(id+"F0.wireOp",EDGE,"E14");var subQ3=sQuery(id+"F2.wireOp",EDGE,"E26.2.0");Q3=makeQuery(id+"F5.boolean.opBoolean","SPLIT",EDGE,{"disambiguationData":[TD([makeQuery(id+"F5.opExtrude","SWEPT_FACE",FACE,{"disambiguationData":[OSD([subQ3])]})])],"derivedFrom":makeQuery(id+"F1.opRevolve","SWEPT_EDGE",EDGE,{"disambiguationData":[OSD([subQ0,subQ1])]})});}
            var Q4;
            {var subQ0=sQuery(id+"F0.wireOp",EDGE,"E3");var subQ1=sQuery(id+"F0.wireOp",EDGE,"E14");var subQ2=sQuery(id+"F2.wireOp",EDGE,"E26.3.0");Q4=makeQuery(id+"F5.boolean.opBoolean","SPLIT",EDGE,{"disambiguationData":[TD([makeQuery(id+"F5.opExtrude","SWEPT_FACE",FACE,{"disambiguationData":[OSD([subQ2])]})])],"derivedFrom":makeQuery(id+"F1.opRevolve","SWEPT_EDGE",EDGE,{"disambiguationData":[OSD([subQ0,subQ1])]})});}
            fillet(context, id + "F9", {"entities" : qUnion([Q0, Q1, Q2, Q3, Q4]), "radius" : 5 * mm, "tangentPropagation" : true, "allowEdgeOverflow" : false});
        }
        {
            var Q0;
            Q0=makeQuery(id+"F5.boolean.opBoolean","INTERSECT",EDGE,{"derivedFrom":[makeQuery(id+"F1.opRevolve","SWEPT_FACE",FACE,{"disambiguationData":[OSD([sQuery(id+"F0.wireOp",EDGE,"E14")])]}),makeQuery(id+"F5.opExtrude","SWEPT_FACE",FACE,{"disambiguationData":[OSD([sQuery(id+"F2.wireOp",EDGE,"E26.1.0")])]})]});
            var Q1;
            Q1=makeQuery(id+"F5.boolean.opBoolean","INTERSECT",EDGE,{"derivedFrom":[makeQuery(id+"F1.opRevolve","SWEPT_FACE",FACE,{"disambiguationData":[OSD([sQuery(id+"F0.wireOp",EDGE,"E14")])]}),makeQuery(id+"F5.opExtrude","SWEPT_FACE",FACE,{"disambiguationData":[OSD([sQuery(id+"F2.wireOp",EDGE,"E26.1.1")])]})]});
            var Q2;
            Q2=makeQuery(id+"F5.boolean.opBoolean","INTERSECT",EDGE,{"derivedFrom":[makeQuery(id+"F1.opRevolve","SWEPT_FACE",FACE,{"disambiguationData":[OSD([sQuery(id+"F0.wireOp",EDGE,"E14")])]}),makeQuery(id+"F5.opExtrude","SWEPT_FACE",FACE,{"disambiguationData":[OSD([sQuery(id+"F2.wireOp",EDGE,"E24")])]})]});
            var Q3;
            Q3=makeQuery(id+"F5.boolean.opBoolean","INTERSECT",EDGE,{"derivedFrom":[makeQuery(id+"F1.opRevolve","SWEPT_FACE",FACE,{"disambiguationData":[OSD([sQuery(id+"F0.wireOp",EDGE,"E14")])]}),makeQuery(id+"F5.opExtrude","SWEPT_FACE",FACE,{"disambiguationData":[OSD([sQuery(id+"F2.wireOp",EDGE,"E25.0.MirrorCS")])]})]});
            var Q4;
            Q4=makeQuery(id+"F5.boolean.opBoolean","INTERSECT",EDGE,{"derivedFrom":[makeQuery(id+"F1.opRevolve","SWEPT_FACE",FACE,{"disambiguationData":[OSD([sQuery(id+"F0.wireOp",EDGE,"E14")])]}),makeQuery(id+"F5.opExtrude","SWEPT_FACE",FACE,{"disambiguationData":[OSD([sQuery(id+"F2.wireOp",EDGE,"E26.4.0")])]})]});
            var Q5;
            Q5=makeQuery(id+"F5.boolean.opBoolean","INTERSECT",EDGE,{"derivedFrom":[makeQuery(id+"F1.opRevolve","SWEPT_FACE",FACE,{"disambiguationData":[OSD([sQuery(id+"F0.wireOp",EDGE,"E14")])]}),makeQuery(id+"F5.opExtrude","SWEPT_FACE",FACE,{"disambiguationData":[OSD([sQuery(id+"F2.wireOp",EDGE,"E26.4.1")])]})]});
            var Q6;
            Q6=makeQuery(id+"F5.boolean.opBoolean","INTERSECT",EDGE,{"derivedFrom":[makeQuery(id+"F1.opRevolve","SWEPT_FACE",FACE,{"disambiguationData":[OSD([sQuery(id+"F0.wireOp",EDGE,"E14")])]}),makeQuery(id+"F5.opExtrude","SWEPT_FACE",FACE,{"disambiguationData":[OSD([sQuery(id+"F2.wireOp",EDGE,"E26.3.0")])]})]});
            var Q7;
            Q7=makeQuery(id+"F5.boolean.opBoolean","INTERSECT",EDGE,{"derivedFrom":[makeQuery(id+"F1.opRevolve","SWEPT_FACE",FACE,{"disambiguationData":[OSD([sQuery(id+"F0.wireOp",EDGE,"E14")])]}),makeQuery(id+"F5.opExtrude","SWEPT_FACE",FACE,{"disambiguationData":[OSD([sQuery(id+"F2.wireOp",EDGE,"E26.3.1")])]})]});
            var Q8;
            Q8=makeQuery(id+"F5.boolean.opBoolean","INTERSECT",EDGE,{"derivedFrom":[makeQuery(id+"F1.opRevolve","SWEPT_FACE",FACE,{"disambiguationData":[OSD([sQuery(id+"F0.wireOp",EDGE,"E14")])]}),makeQuery(id+"F5.opExtrude","SWEPT_FACE",FACE,{"disambiguationData":[OSD([sQuery(id+"F2.wireOp",EDGE,"E26.2.0")])]})]});
            var Q9;
            Q9=makeQuery(id+"F5.boolean.opBoolean","INTERSECT",EDGE,{"derivedFrom":[makeQuery(id+"F1.opRevolve","SWEPT_FACE",FACE,{"disambiguationData":[OSD([sQuery(id+"F0.wireOp",EDGE,"E14")])]}),makeQuery(id+"F5.opExtrude","SWEPT_FACE",FACE,{"disambiguationData":[OSD([sQuery(id+"F2.wireOp",EDGE,"E26.2.1")])]})]});
            chamfer(context, id + "F10", {"entities" : qUnion([Q0, Q1, Q2, Q3, Q4, Q5, Q6, Q7, Q8, Q9]), "width" : 0.5 * mm, "tangentPropagation" : true});
        }
        {
            var Q0;
            Q0=makeQuery(id+"F6.boolean.opBoolean","COPY",EDGE,{"derivedFrom":makeQuery(id+"F6.opExtrude","CAP_EDGE",EDGE,{"disambiguationData":[OSD([sQuery(id+"F3.wireOp",EDGE,"E34.1.1")])],"isStart":false})});
            var Q1;
            Q1=makeQuery(id+"F6.boolean.opBoolean","COPY",EDGE,{"derivedFrom":makeQuery(id+"F6.opExtrude","CAP_EDGE",EDGE,{"disambiguationData":[OSD([sQuery(id+"F3.wireOp",EDGE,"E34.1.0")])],"isStart":false})});
            var Q2;
            Q2=makeQuery(id+"F6.boolean.opBoolean","COPY",EDGE,{"derivedFrom":makeQuery(id+"F6.opExtrude","CAP_EDGE",EDGE,{"disambiguationData":[OSD([sQuery(id+"F3.wireOp",EDGE,"E34.2.1")])],"isStart":false})});
            var Q3;
            Q3=makeQuery(id+"F6.boolean.opBoolean","COPY",EDGE,{"derivedFrom":makeQuery(id+"F6.opExtrude","CAP_EDGE",EDGE,{"disambiguationData":[OSD([sQuery(id+"F3.wireOp",EDGE,"E34.2.0")])],"isStart":false})});
            var Q4;
            Q4=makeQuery(id+"F6.boolean.opBoolean","COPY",EDGE,{"derivedFrom":makeQuery(id+"F6.opExtrude","CAP_EDGE",EDGE,{"disambiguationData":[OSD([sQuery(id+"F3.wireOp",EDGE,"E34.3.1")])],"isStart":false})});
            var Q5;
            {var subQ0=sQuery(id+"F0.wireOp",EDGE,"E2");var subQ1=sQuery(id+"F0.wireOp",EDGE,"E3");var subQ3=sQuery(id+"F3.wireOp",EDGE,"E34.2.0");Q5=makeQuery(id+"F6.boolean.opBoolean","SPLIT",EDGE,{"disambiguationData":[TD([makeQuery(id+"F6.opExtrude","SWEPT_FACE",FACE,{"disambiguationData":[OSD([subQ3])]})])],"derivedFrom":makeQuery(id+"F1.opRevolve","SWEPT_EDGE",EDGE,{"disambiguationData":[OSD([subQ0,subQ1])]})});}
            var Q6;
            {var subQ0=sQuery(id+"F0.wireOp",EDGE,"E2");var subQ1=sQuery(id+"F0.wireOp",EDGE,"E3");var subQ3=sQuery(id+"F3.wireOp",EDGE,"E34.1.0");Q6=makeQuery(id+"F6.boolean.opBoolean","SPLIT",EDGE,{"disambiguationData":[TD([makeQuery(id+"F6.opExtrude","SWEPT_FACE",FACE,{"disambiguationData":[OSD([subQ3])]})])],"derivedFrom":makeQuery(id+"F1.opRevolve","SWEPT_EDGE",EDGE,{"disambiguationData":[OSD([subQ0,subQ1])]})});}
            var Q7;
            Q7=makeQuery(id+"F6.boolean.opBoolean","COPY",EDGE,{"derivedFrom":makeQuery(id+"F6.opExtrude","CAP_EDGE",EDGE,{"disambiguationData":[OSD([sQuery(id+"F3.wireOp",EDGE,"E34.3.0")])],"isStart":false})});
            var Q8;
            {var subQ0=sQuery(id+"F0.wireOp",EDGE,"E2");var subQ1=sQuery(id+"F0.wireOp",EDGE,"E3");var subQ6=sQuery(id+"F3.wireOp",EDGE,"E34.3.0");Q8=makeQuery(id+"F6.boolean.opBoolean","SPLIT",EDGE,{"disambiguationData":[TD([makeQuery(id+"F6.opExtrude","SWEPT_FACE",FACE,{"disambiguationData":[OSD([subQ6])]})])],"derivedFrom":makeQuery(id+"F1.opRevolve","SWEPT_EDGE",EDGE,{"disambiguationData":[OSD([subQ0,subQ1])]})});}
            var Q9;
            Q9=makeQuery(id+"F6.boolean.opBoolean","COPY",EDGE,{"derivedFrom":makeQuery(id+"F6.opExtrude","CAP_EDGE",EDGE,{"disambiguationData":[OSD([sQuery(id+"F3.wireOp",EDGE,"E34.4.1")])],"isStart":false})});
            var Q10;
            Q10=makeQuery(id+"F6.boolean.opBoolean","COPY",EDGE,{"derivedFrom":makeQuery(id+"F6.opExtrude","CAP_EDGE",EDGE,{"disambiguationData":[OSD([sQuery(id+"F3.wireOp",EDGE,"E34.4.0")])],"isStart":false})});
            var Q11;
            {var subQ0=sQuery(id+"F0.wireOp",EDGE,"E2");var subQ1=sQuery(id+"F0.wireOp",EDGE,"E3");var subQ3=sQuery(id+"F3.wireOp",EDGE,"E34.4.0");Q11=makeQuery(id+"F6.boolean.opBoolean","SPLIT",EDGE,{"disambiguationData":[TD([makeQuery(id+"F6.opExtrude","SWEPT_FACE",FACE,{"disambiguationData":[OSD([subQ3])]})])],"derivedFrom":makeQuery(id+"F1.opRevolve","SWEPT_EDGE",EDGE,{"disambiguationData":[OSD([subQ0,subQ1])]})});}
            var Q12;
            Q12=makeQuery(id+"F6.boolean.opBoolean","COPY",EDGE,{"derivedFrom":makeQuery(id+"F6.opExtrude","CAP_EDGE",EDGE,{"disambiguationData":[OSD([sQuery(id+"F3.wireOp",EDGE,"E34.5.1")])],"isStart":false})});
            var Q13;
            Q13=makeQuery(id+"F6.boolean.opBoolean","COPY",EDGE,{"derivedFrom":makeQuery(id+"F6.opExtrude","CAP_EDGE",EDGE,{"disambiguationData":[OSD([sQuery(id+"F3.wireOp",EDGE,"E34.5.0")])],"isStart":false})});
            var Q14;
            {var subQ0=sQuery(id+"F0.wireOp",EDGE,"E2");var subQ1=sQuery(id+"F0.wireOp",EDGE,"E3");var subQ2=sQuery(id+"F3.wireOp",EDGE,"E34.5.0");Q14=makeQuery(id+"F6.boolean.opBoolean","SPLIT",EDGE,{"disambiguationData":[TD([makeQuery(id+"F6.opExtrude","SWEPT_FACE",FACE,{"disambiguationData":[OSD([subQ2])]})])],"derivedFrom":makeQuery(id+"F1.opRevolve","SWEPT_EDGE",EDGE,{"disambiguationData":[OSD([subQ0,subQ1])]})});}
            var Q15;
            Q15=makeQuery(id+"F6.boolean.opBoolean","COPY",EDGE,{"derivedFrom":makeQuery(id+"F6.opExtrude","CAP_EDGE",EDGE,{"disambiguationData":[OSD([sQuery(id+"F3.wireOp",EDGE,"E34.6.1")])],"isStart":false})});
            var Q16;
            Q16=makeQuery(id+"F6.boolean.opBoolean","COPY",EDGE,{"derivedFrom":makeQuery(id+"F6.opExtrude","CAP_EDGE",EDGE,{"disambiguationData":[OSD([sQuery(id+"F3.wireOp",EDGE,"E34.6.0")])],"isStart":false})});
            var Q17;
            {var subQ0=sQuery(id+"F0.wireOp",EDGE,"E2");var subQ1=sQuery(id+"F0.wireOp",EDGE,"E3");var subQ6=sQuery(id+"F3.wireOp",EDGE,"E34.6.0");Q17=makeQuery(id+"F6.boolean.opBoolean","SPLIT",EDGE,{"disambiguationData":[TD([makeQuery(id+"F6.opExtrude","SWEPT_FACE",FACE,{"disambiguationData":[OSD([subQ6])]})])],"derivedFrom":makeQuery(id+"F1.opRevolve","SWEPT_EDGE",EDGE,{"disambiguationData":[OSD([subQ0,subQ1])]})});}
            var Q18;
            Q18=makeQuery(id+"F6.boolean.opBoolean","COPY",EDGE,{"derivedFrom":makeQuery(id+"F6.opExtrude","CAP_EDGE",EDGE,{"disambiguationData":[OSD([sQuery(id+"F3.wireOp",EDGE,"E34.7.1")])],"isStart":false})});
            var Q19;
            Q19=makeQuery(id+"F6.boolean.opBoolean","COPY",EDGE,{"derivedFrom":makeQuery(id+"F6.opExtrude","CAP_EDGE",EDGE,{"disambiguationData":[OSD([sQuery(id+"F3.wireOp",EDGE,"E34.7.0")])],"isStart":false})});
            var Q20;
            {var subQ0=sQuery(id+"F0.wireOp",EDGE,"E2");var subQ1=sQuery(id+"F0.wireOp",EDGE,"E3");var subQ3=sQuery(id+"F3.wireOp",EDGE,"E34.7.0");Q20=makeQuery(id+"F6.boolean.opBoolean","SPLIT",EDGE,{"disambiguationData":[TD([makeQuery(id+"F6.opExtrude","SWEPT_FACE",FACE,{"disambiguationData":[OSD([subQ3])]})])],"derivedFrom":makeQuery(id+"F1.opRevolve","SWEPT_EDGE",EDGE,{"disambiguationData":[OSD([subQ0,subQ1])]})});}
            var Q21;
            Q21=makeQuery(id+"F6.boolean.opBoolean","COPY",EDGE,{"derivedFrom":makeQuery(id+"F6.opExtrude","CAP_EDGE",EDGE,{"disambiguationData":[OSD([sQuery(id+"F3.wireOp",EDGE,"E34.8.1")])],"isStart":false})});
            var Q22;
            Q22=makeQuery(id+"F6.boolean.opBoolean","COPY",EDGE,{"derivedFrom":makeQuery(id+"F6.opExtrude","CAP_EDGE",EDGE,{"disambiguationData":[OSD([sQuery(id+"F3.wireOp",EDGE,"E34.8.0")])],"isStart":false})});
            var Q23;
            {var subQ0=sQuery(id+"F0.wireOp",EDGE,"E2");var subQ1=sQuery(id+"F0.wireOp",EDGE,"E3");var subQ3=sQuery(id+"F3.wireOp",EDGE,"E34.8.0");Q23=makeQuery(id+"F6.boolean.opBoolean","SPLIT",EDGE,{"disambiguationData":[TD([makeQuery(id+"F6.opExtrude","SWEPT_FACE",FACE,{"disambiguationData":[OSD([subQ3])]})])],"derivedFrom":makeQuery(id+"F1.opRevolve","SWEPT_EDGE",EDGE,{"disambiguationData":[OSD([subQ0,subQ1])]})});}
            var Q24;
            Q24=makeQuery(id+"F6.boolean.opBoolean","COPY",EDGE,{"derivedFrom":makeQuery(id+"F6.opExtrude","CAP_EDGE",EDGE,{"disambiguationData":[OSD([sQuery(id+"F3.wireOp",EDGE,"E34.9.1")])],"isStart":false})});
            var Q25;
            {var subQ0=sQuery(id+"F0.wireOp",EDGE,"E2");var subQ1=sQuery(id+"F0.wireOp",EDGE,"E3");var subQ4=sQuery(id+"F3.wireOp",EDGE,"E33.0.MirrorCS");Q25=makeQuery(id+"F6.boolean.opBoolean","SPLIT",EDGE,{"disambiguationData":[TD([makeQuery(id+"F6.opExtrude","SWEPT_FACE",FACE,{"disambiguationData":[OSD([subQ4])]})])],"derivedFrom":makeQuery(id+"F1.opRevolve","SWEPT_EDGE",EDGE,{"disambiguationData":[OSD([subQ0,subQ1])]})});}
            var Q26;
            Q26=makeQuery(id+"F6.boolean.opBoolean","COPY",EDGE,{"derivedFrom":makeQuery(id+"F6.opExtrude","CAP_EDGE",EDGE,{"disambiguationData":[OSD([sQuery(id+"F3.wireOp",EDGE,"E33.0.MirrorCS")])],"isStart":false})});
            var Q27;
            Q27=makeQuery(id+"F6.boolean.opBoolean","COPY",EDGE,{"derivedFrom":makeQuery(id+"F6.opExtrude","CAP_EDGE",EDGE,{"disambiguationData":[OSD([sQuery(id+"F3.wireOp",EDGE,"E34.9.0")])],"isStart":false})});
            var Q28;
            Q28=makeQuery(id+"F6.boolean.opBoolean","COPY",EDGE,{"derivedFrom":makeQuery(id+"F6.opExtrude","CAP_EDGE",EDGE,{"disambiguationData":[OSD([sQuery(id+"F3.wireOp",EDGE,"E32")])],"isStart":false})});
            var Q29;
            {var subQ0=sQuery(id+"F0.wireOp",EDGE,"E2");var subQ1=sQuery(id+"F0.wireOp",EDGE,"E3");var subQ5=sQuery(id+"F3.wireOp",EDGE,"E32");Q29=makeQuery(id+"F6.boolean.opBoolean","SPLIT",EDGE,{"disambiguationData":[TD([makeQuery(id+"F6.opExtrude","SWEPT_FACE",FACE,{"disambiguationData":[OSD([subQ5])]})])],"derivedFrom":makeQuery(id+"F1.opRevolve","SWEPT_EDGE",EDGE,{"disambiguationData":[OSD([subQ0,subQ1])]})});}
            var Q30;
            Q30=makeQuery(id+"F6.boolean.opBoolean","COPY",EDGE,{"derivedFrom":makeQuery(id+"F6.opExtrude","CAP_EDGE",EDGE,{"disambiguationData":[OSD([sQuery(id+"F3.wireOp",EDGE,"E34.3.0")])],"isStart":true})});
            var Q31;
            Q31=makeQuery(id+"F6.boolean.opBoolean","COPY",EDGE,{"derivedFrom":makeQuery(id+"F6.opExtrude","CAP_EDGE",EDGE,{"disambiguationData":[OSD([sQuery(id+"F3.wireOp",EDGE,"E34.4.1")])],"isStart":true})});
            var Q32;
            Q32=makeQuery(id+"F6.boolean.opBoolean","COPY",EDGE,{"derivedFrom":makeQuery(id+"F6.opExtrude","CAP_EDGE",EDGE,{"disambiguationData":[OSD([sQuery(id+"F3.wireOp",EDGE,"E34.3.1")])],"isStart":true})});
            var Q33;
            Q33=makeQuery(id+"F6.boolean.opBoolean","COPY",EDGE,{"derivedFrom":makeQuery(id+"F6.opExtrude","CAP_EDGE",EDGE,{"disambiguationData":[OSD([sQuery(id+"F3.wireOp",EDGE,"E34.2.0")])],"isStart":true})});
            var Q34;
            Q34=makeQuery(id+"F6.boolean.opBoolean","COPY",EDGE,{"derivedFrom":makeQuery(id+"F6.opExtrude","CAP_EDGE",EDGE,{"disambiguationData":[OSD([sQuery(id+"F3.wireOp",EDGE,"E34.2.1")])],"isStart":true})});
            var Q35;
            Q35=makeQuery(id+"F6.boolean.opBoolean","COPY",EDGE,{"derivedFrom":makeQuery(id+"F6.opExtrude","CAP_EDGE",EDGE,{"disambiguationData":[OSD([sQuery(id+"F3.wireOp",EDGE,"E34.1.0")])],"isStart":true})});
            var Q36;
            Q36=makeQuery(id+"F6.boolean.opBoolean","COPY",EDGE,{"derivedFrom":makeQuery(id+"F6.opExtrude","CAP_EDGE",EDGE,{"disambiguationData":[OSD([sQuery(id+"F3.wireOp",EDGE,"E34.1.1")])],"isStart":true})});
            var Q37;
            Q37=makeQuery(id+"F6.boolean.opBoolean","COPY",EDGE,{"derivedFrom":makeQuery(id+"F6.opExtrude","CAP_EDGE",EDGE,{"disambiguationData":[OSD([sQuery(id+"F3.wireOp",EDGE,"E32")])],"isStart":true})});
            var Q38;
            Q38=makeQuery(id+"F6.boolean.opBoolean","COPY",EDGE,{"derivedFrom":makeQuery(id+"F6.opExtrude","CAP_EDGE",EDGE,{"disambiguationData":[OSD([sQuery(id+"F3.wireOp",EDGE,"E33.0.MirrorCS")])],"isStart":true})});
            var Q39;
            Q39=makeQuery(id+"F6.boolean.opBoolean","COPY",EDGE,{"derivedFrom":makeQuery(id+"F6.opExtrude","CAP_EDGE",EDGE,{"disambiguationData":[OSD([sQuery(id+"F3.wireOp",EDGE,"E34.9.0")])],"isStart":true})});
            var Q40;
            Q40=makeQuery(id+"F6.boolean.opBoolean","COPY",EDGE,{"derivedFrom":makeQuery(id+"F6.opExtrude","CAP_EDGE",EDGE,{"disambiguationData":[OSD([sQuery(id+"F3.wireOp",EDGE,"E34.9.1")])],"isStart":true})});
            var Q41;
            Q41=makeQuery(id+"F6.boolean.opBoolean","COPY",EDGE,{"derivedFrom":makeQuery(id+"F6.opExtrude","CAP_EDGE",EDGE,{"disambiguationData":[OSD([sQuery(id+"F3.wireOp",EDGE,"E34.8.0")])],"isStart":true})});
            var Q42;
            Q42=makeQuery(id+"F6.boolean.opBoolean","COPY",EDGE,{"derivedFrom":makeQuery(id+"F6.opExtrude","CAP_EDGE",EDGE,{"disambiguationData":[OSD([sQuery(id+"F3.wireOp",EDGE,"E34.8.1")])],"isStart":true})});
            var Q43;
            Q43=makeQuery(id+"F6.boolean.opBoolean","COPY",EDGE,{"derivedFrom":makeQuery(id+"F6.opExtrude","CAP_EDGE",EDGE,{"disambiguationData":[OSD([sQuery(id+"F3.wireOp",EDGE,"E34.7.0")])],"isStart":true})});
            var Q44;
            Q44=makeQuery(id+"F6.boolean.opBoolean","COPY",EDGE,{"derivedFrom":makeQuery(id+"F6.opExtrude","CAP_EDGE",EDGE,{"disambiguationData":[OSD([sQuery(id+"F3.wireOp",EDGE,"E34.7.1")])],"isStart":true})});
            var Q45;
            Q45=makeQuery(id+"F6.boolean.opBoolean","COPY",EDGE,{"derivedFrom":makeQuery(id+"F6.opExtrude","CAP_EDGE",EDGE,{"disambiguationData":[OSD([sQuery(id+"F3.wireOp",EDGE,"E34.6.0")])],"isStart":true})});
            var Q46;
            Q46=makeQuery(id+"F6.boolean.opBoolean","COPY",EDGE,{"derivedFrom":makeQuery(id+"F6.opExtrude","CAP_EDGE",EDGE,{"disambiguationData":[OSD([sQuery(id+"F3.wireOp",EDGE,"E34.6.1")])],"isStart":true})});
            var Q47;
            Q47=makeQuery(id+"F6.boolean.opBoolean","COPY",EDGE,{"derivedFrom":makeQuery(id+"F6.opExtrude","CAP_EDGE",EDGE,{"disambiguationData":[OSD([sQuery(id+"F3.wireOp",EDGE,"E34.5.0")])],"isStart":true})});
            var Q48;
            Q48=makeQuery(id+"F6.boolean.opBoolean","COPY",EDGE,{"derivedFrom":makeQuery(id+"F6.opExtrude","CAP_EDGE",EDGE,{"disambiguationData":[OSD([sQuery(id+"F3.wireOp",EDGE,"E34.5.1")])],"isStart":true})});
            var Q49;
            Q49=makeQuery(id+"F6.boolean.opBoolean","COPY",EDGE,{"derivedFrom":makeQuery(id+"F6.opExtrude","CAP_EDGE",EDGE,{"disambiguationData":[OSD([sQuery(id+"F3.wireOp",EDGE,"E34.4.0")])],"isStart":true})});
            fillet(context, id + "F11", {"entities" : qUnion([Q0, Q1, Q2, Q3, Q4, Q5, Q6, Q7, Q8, Q9, Q10, Q11, Q12, Q13, Q14, Q15, Q16, Q17, Q18, Q19, Q20, Q21, Q22, Q23, Q24, Q25, Q26, Q27, Q28, Q29, Q30, Q31, Q32, Q33, Q34, Q35, Q36, Q37, Q38, Q39, Q40, Q41, Q42, Q43, Q44, Q45, Q46, Q47, Q48, Q49]), "radius" : 1.5 * mm, "tangentPropagation" : true, "allowEdgeOverflow" : false});
        }
    });
